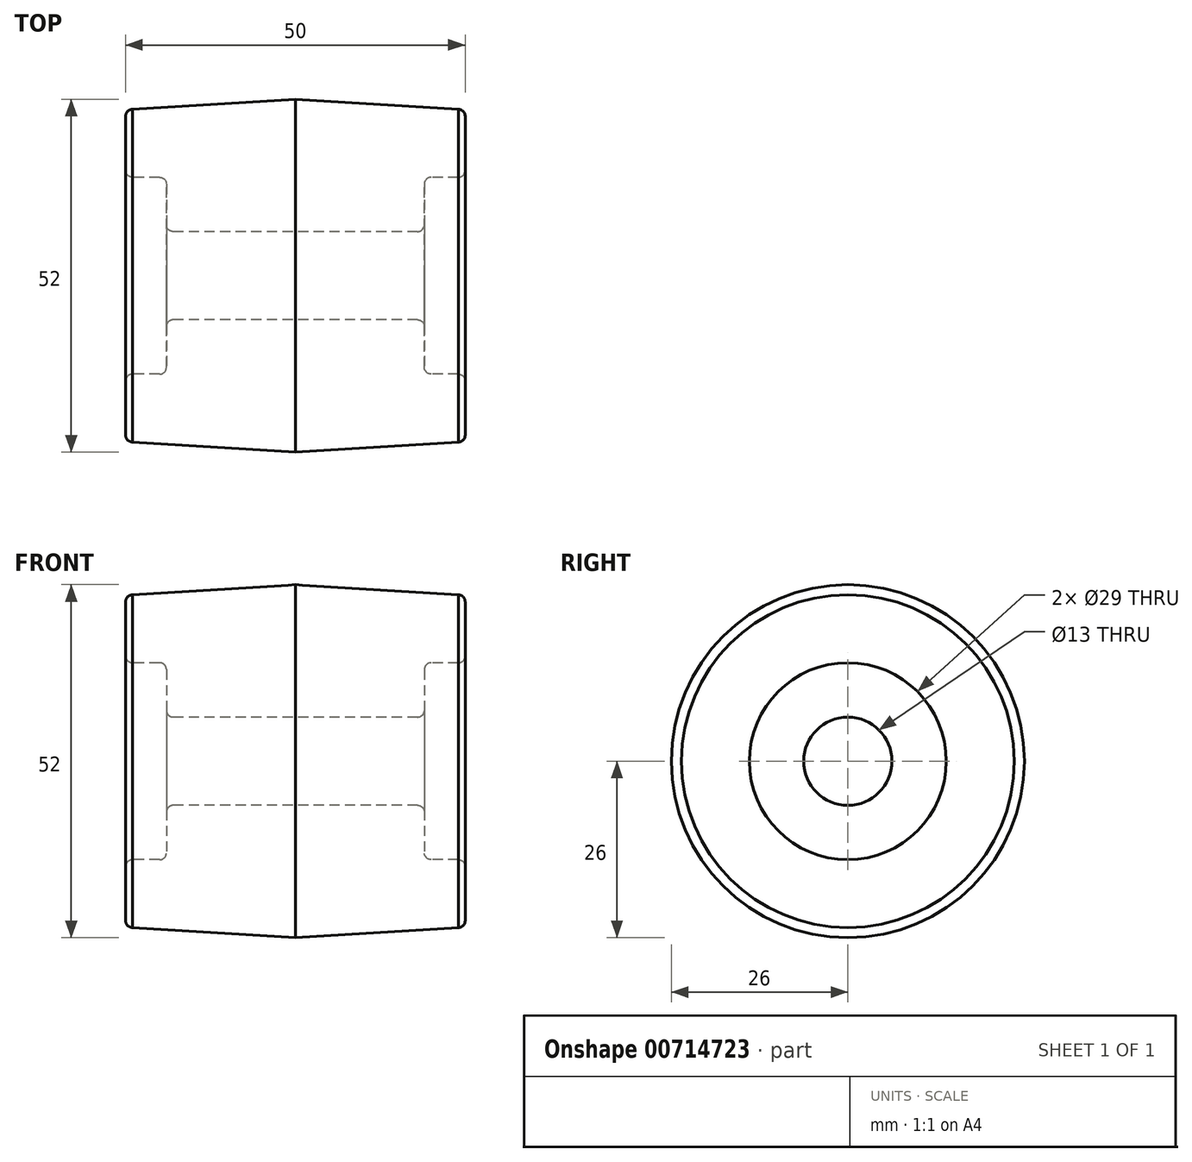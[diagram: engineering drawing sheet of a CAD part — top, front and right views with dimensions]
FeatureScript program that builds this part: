
annotation { "Feature Type Name" : "Feature", "Feature Type Description" : "" }
export const myFeature = defineFeature(function(context is Context, id is Id, definition is map)
    precondition{}
    {
        {
            var Q0;
            Q0=qCreatedBy(makeId("Top.planeOp"),FACE);
            var sketch = newSketch(context, id + "F0", { "sketchPlane" : qUnion([Q0])});
            skLineSegment(sketch, "E0", {"start": v(0, 72.5) * mm, "end": v(0, -75.45) * mm, "construction": true});
            skLineSegment(sketch, "E1", {"start": v(-71.57, 0) * mm, "end": v(74.16, 0) * mm, "construction": true});
            skLineSegment(sketch, "E2", {"start": v(0, -6.5) * mm, "end": v(-18, -6.5) * mm});
            skLineSegment(sketch, "E3.MirrorCS", {"start": v(0, -6.5) * mm, "end": v(19, -6.5) * mm});
            skLineSegment(sketch, "E4", {"start": v(-19, -7.5) * mm, "end": v(-19, -13.5) * mm});
            skLineSegment(sketch, "E5", {"start": v(-20, -14.5) * mm, "end": v(-24, -14.5) * mm});
            skLineSegment(sketch, "E6", {"start": v(-25, -15.5) * mm, "end": v(-25, -23.5) * mm});
            skLineSegment(sketch, "E7", {"start": v(-24, -24.5) * mm, "end": v(0, -24.5) * mm});
            skPoint(sketch, "E8.visualSharp", {"position": v(-25, -24.5) * mm});
            skArc(sketch, "E8.filletArc", {"start": v(-25, -23.5) * mm, "mid": v(-24.7, -24.2) * mm, "end": v(-24, -24.5) * mm});
            skPoint(sketch, "E9.visualSharp", {"position": v(-25, -14.5) * mm});
            skArc(sketch, "E9.filletArc", {"start": v(-24, -14.5) * mm, "mid": v(-24.7, -14.8) * mm, "end": v(-25, -15.5) * mm});
            skPoint(sketch, "E10.visualSharp", {"position": v(-19, -14.5) * mm});
            skArc(sketch, "E10.filletArc", {"start": v(-20, -14.5) * mm, "mid": v(-19.3, -14.2) * mm, "end": v(-19, -13.5) * mm});
            skPoint(sketch, "E11.visualSharp", {"position": v(-19, -6.5) * mm});
            skArc(sketch, "E11.filletArc", {"start": v(-18, -6.5) * mm, "mid": v(-18.7, -6.8) * mm, "end": v(-19, -7.5) * mm});
            skLineSegment(sketch, "E12.MirrorCS", {"start": v(0, -6.5) * mm, "end": v(18, -6.5) * mm});
            skArc(sketch, "E13.MirrorCS", {"start": v(18, -6.5) * mm, "mid": v(18.7, -6.8) * mm, "end": v(19, -7.5) * mm});
            skLineSegment(sketch, "E14.MirrorCS", {"start": v(20, -14.5) * mm, "end": v(24, -14.5) * mm});
            skArc(sketch, "E15.MirrorCS", {"start": v(20, -14.5) * mm, "mid": v(19.3, -14.2) * mm, "end": v(19, -13.5) * mm});
            skLineSegment(sketch, "E16.MirrorCS", {"start": v(19, -7.5) * mm, "end": v(19, -13.5) * mm});
            skArc(sketch, "E17.MirrorCS", {"start": v(24, -14.5) * mm, "mid": v(24.7, -14.8) * mm, "end": v(25, -15.5) * mm});
            skArc(sketch, "E18.MirrorCS", {"start": v(25, -23.5) * mm, "mid": v(24.7, -24.2) * mm, "end": v(24, -24.5) * mm});
            skLineSegment(sketch, "E19.MirrorCS", {"start": v(24, -24.5) * mm, "end": v(0, -24.5) * mm});
            skLineSegment(sketch, "E20.MirrorCS", {"start": v(25, -15.5) * mm, "end": v(25, -23.5) * mm});
            skLineSegment(sketch, "E21", {"start": v(0, -24.5) * mm, "end": v(0, -26) * mm});
            skLineSegment(sketch, "E22", {"start": v(0, -26) * mm, "end": v(24, -24.5) * mm});
            skLineSegment(sketch, "E23.MirrorCS", {"start": v(0, -26) * mm, "end": v(-24, -24.5) * mm});
            skSolve(sketch);
        }
        {
            var Q0;
            Q0=makeQuery(id+"F0.imprint","IMPRINT",FACE,{"disambiguationData":[TD([[makeQuery(id+"F0.imprint","IMPRINT",EDGE,{"derivedFrom":sQuery(id+"F0.wireOp",EDGE,"E2")}),1.0]])]});
            var Q1;
            Q1=makeQuery(id+"F0.imprint","IMPRINT",FACE,{"disambiguationData":[TD([[makeQuery(id+"F0.imprint","IMPRINT",EDGE,{"derivedFrom":sQuery(id+"F0.wireOp",EDGE,"E19.MirrorCS")}),1.0]])]});
            var Q2;
            Q2=makeQuery(id+"F0.imprint","IMPRINT",FACE,{"disambiguationData":[TD([[makeQuery(id+"F0.imprint","IMPRINT",EDGE,{"derivedFrom":sQuery(id+"F0.wireOp",EDGE,"E7")}),-1.0]])]});
            var Q3;
            Q3=sQuery(id+"F0.wireOp",EDGE,"E1");
            revolve(context, id + "F1", {"surfaceOperationType" : NewSurfaceOperationType.NEW, "entities" : qUnion([Q0, Q1, Q2]), "axis" : qUnion([Q3]), "revolveType" : RevolveType.FULL});
        }
    });
